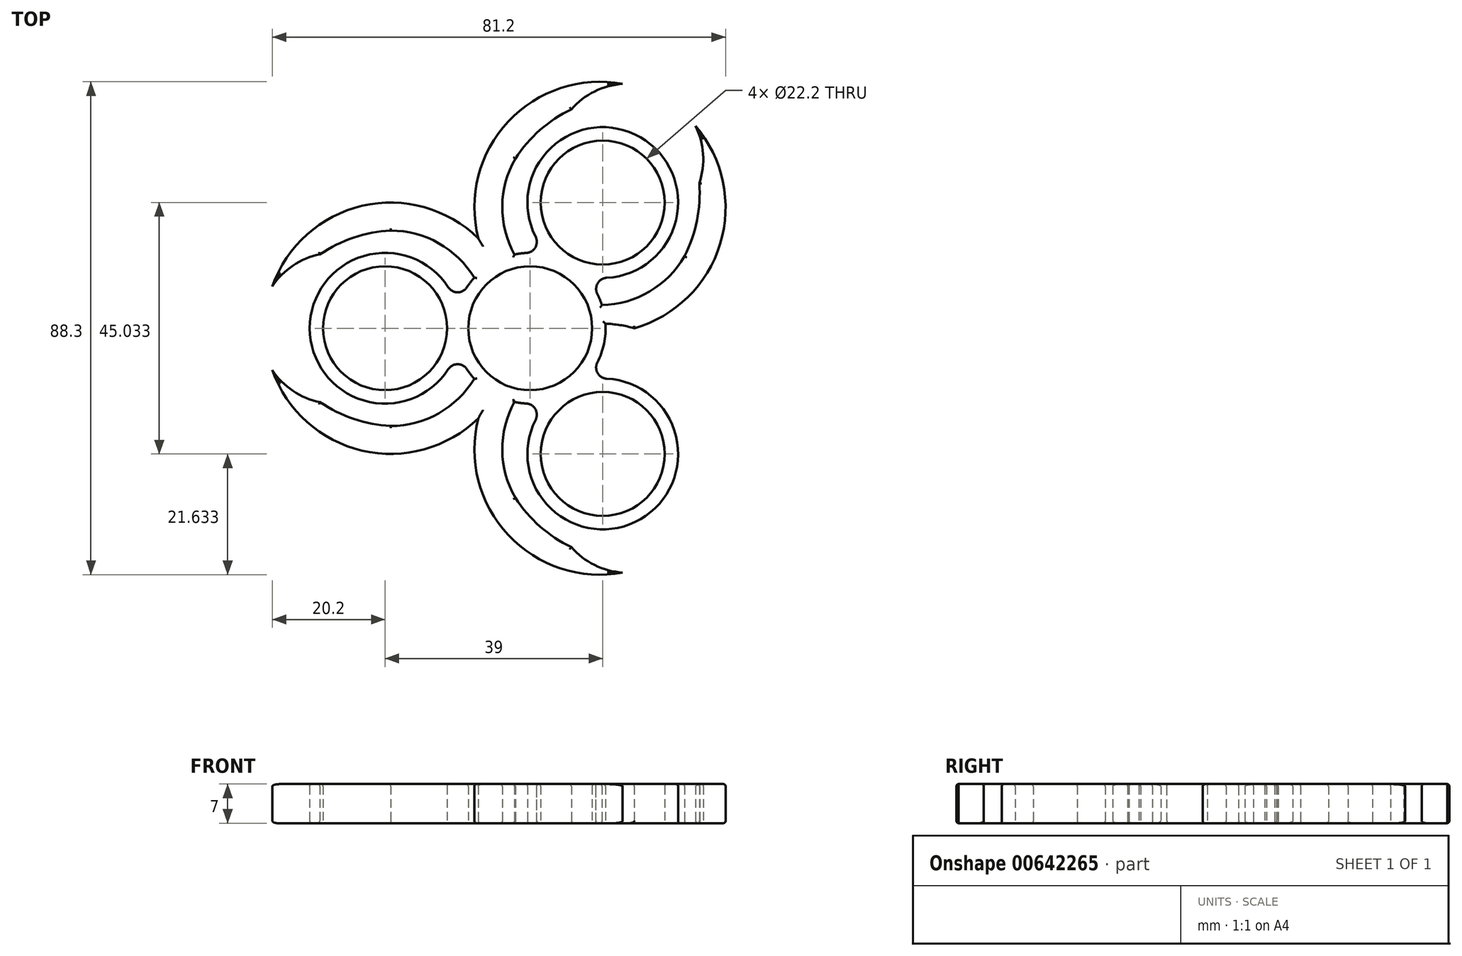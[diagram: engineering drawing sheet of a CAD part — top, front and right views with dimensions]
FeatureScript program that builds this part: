
annotation { "Feature Type Name" : "Feature", "Feature Type Description" : "" }
export const myFeature = defineFeature(function(context is Context, id is Id, definition is map)
    precondition{}
    {
        {
            var Q0;
            Q0=qCreatedBy(makeId("Top.planeOp"),FACE);
            var sketch = newSketch(context, id + "F0", { "sketchPlane" : qUnion([Q0])});
            skLineSegment(sketch, "E0", {"start": v(0, 0) * mm, "end": v(-25, 0) * mm, "construction": true});
            skArc(sketch, "E1", {"start": v(-25, -17.5) * mm, "mid": v(-7.5, 0) * mm, "end": v(-25, 17.5) * mm});
            skCircle(sketch, "E2", {"center": v(-25, 0) * mm, "radius": 22.5 * mm});
            skLineSegment(sketch, "E3", {"start": v(-25, 0) * mm, "end": v(-25, 22.5) * mm, "construction": true});
            skLineSegment(sketch, "E4", {"start": v(-25, 0) * mm, "end": v(-25, -22.5) * mm, "construction": true});
            skLineSegment(sketch, "E5", {"start": v(-25, 0) * mm, "end": v(-47.5, 0) * mm, "construction": true});
            skArc(sketch, "E6", {"start": v(-25, 17.5) * mm, "mid": v(-38.99, 12.27) * mm, "end": v(-47.5, 0) * mm});
            skArc(sketch, "E7.MirrorCS", {"start": v(-25, -17.5) * mm, "mid": v(-38.99, -12.27) * mm, "end": v(-47.5, 0) * mm});
            skArc(sketch, "E8.1.0", {"start": v(27.66, -12.9) * mm, "mid": v(30.12, -27.63) * mm, "end": v(23.75, -41.14) * mm});
            skLineSegment(sketch, "E8.1.1", {"start": v(12.5, -21.65) * mm, "end": v(-6.99, -32.9) * mm, "construction": true});
            skArc(sketch, "E8.1.2", {"start": v(-2.66, -30.4) * mm, "mid": v(8.87, -39.9) * mm, "end": v(23.75, -41.14) * mm});
            skLineSegment(sketch, "E8.1.3", {"start": v(12.5, -21.65) * mm, "end": v(23.75, -41.14) * mm, "construction": true});
            skArc(sketch, "E8.1.4", {"start": v(27.66, -12.9) * mm, "mid": v(3.75, -6.5) * mm, "end": v(-2.66, -30.4) * mm});
            skArc(sketch, "E8.1.5", {"start": v(-9.31, -16.13) * mm, "mid": v(33.52, -29.66) * mm, "end": v(-7.45, -11.26) * mm});
            skLineSegment(sketch, "E8.1.6", {"start": v(12.5, -21.65) * mm, "end": v(31.99, -10.4) * mm, "construction": true});
            skArc(sketch, "E8.2.0", {"start": v(-2.66, 30.4) * mm, "mid": v(8.87, 39.9) * mm, "end": v(23.75, 41.14) * mm});
            skLineSegment(sketch, "E8.2.1", {"start": v(12.5, 21.65) * mm, "end": v(31.99, 10.4) * mm, "construction": true});
            skArc(sketch, "E8.2.2", {"start": v(27.66, 12.9) * mm, "mid": v(30.12, 27.63) * mm, "end": v(23.75, 41.14) * mm});
            skLineSegment(sketch, "E8.2.3", {"start": v(12.5, 21.65) * mm, "end": v(23.75, 41.14) * mm, "construction": true});
            skArc(sketch, "E8.2.4", {"start": v(-2.66, 30.4) * mm, "mid": v(3.75, 6.5) * mm, "end": v(27.66, 12.9) * mm});
            skArc(sketch, "E8.2.5", {"start": v(-7.45, 11.26) * mm, "mid": v(1.25, 2.17) * mm, "end": v(13.47, -0.83) * mm});
            skLineSegment(sketch, "E8.2.6", {"start": v(12.5, 21.65) * mm, "end": v(-6.99, 32.9) * mm, "construction": true});
            skPoint(sketch, "E8.center", {"position": v(0, 0) * mm});
            skCircle(sketch, "E9.0.0", {"center": v(0, 0) * mm, "radius": 13.5 * mm});
            skCircle(sketch, "E10.0.0", {"center": v(-35, 0) * mm, "radius": 13.5 * mm});
            skCircle(sketch, "E11.0.0", {"center": v(17.5, 30.31) * mm, "radius": 13.5 * mm});
            skCircle(sketch, "E12.0.0", {"center": v(17.5, -30.31) * mm, "radius": 13.5 * mm});
            skCircle(sketch, "E13.0", {"center": v(0, 0) * mm, "radius": 11 * mm});
            skArc(sketch, "E14.trimOffspring", {"start": v(18.62, 0) * mm, "mid": v(23.75, 41.14) * mm, "end": v(-9.31, 16.13) * mm});
            skSolve(sketch);
        }
        {
            var Q0;
            Q0=qCreatedBy(makeId("Top.planeOp"),FACE);
            var sketch = newSketch(context, id + "F1", { "sketchPlane" : qUnion([Q0])});
            skCircle(sketch, "E15", {"center": v(0, 0) * mm, "radius": 11.1 * mm});
            skCircle(sketch, "E16", {"center": v(0, 0) * mm, "radius": 13.5 * mm});
            skLineSegment(sketch, "E17", {"start": v(0, 0) * mm, "end": v(-26, 0) * mm, "construction": true});
            skCircle(sketch, "E18", {"center": v(-26, 0) * mm, "radius": 11.1 * mm});
            skCircle(sketch, "E19", {"center": v(-26, 0) * mm, "radius": 13.5 * mm});
            skCircle(sketch, "E20.1.0", {"center": v(13, -22.52) * mm, "radius": 11.1 * mm});
            skCircle(sketch, "E20.1.1", {"center": v(13, -22.52) * mm, "radius": 13.5 * mm});
            skCircle(sketch, "E20.2.0", {"center": v(13, 22.52) * mm, "radius": 11.1 * mm});
            skCircle(sketch, "E20.2.1", {"center": v(13, 22.52) * mm, "radius": 13.5 * mm});
            skSolve(sketch);
        }
        {
            var Q0;
            Q0=makeQuery(id+"F1.imprint","IMPRINT",FACE,{"disambiguationData":[TD([[makeQuery(id+"F1.imprint","IMPRINT",EDGE,{"derivedFrom":sQuery(id+"F1.wireOp",EDGE,"E15")}),-1.0]])]});
            var Q1;
            {var subQ0=sQuery(id+"F1.wireOp",EDGE,"E19");var subQ1=sQuery(id+"F1.wireOp",EDGE,"E16");var subQ2=makeQuery(id+"F1.imprint","INTERSECT",VERTEX,{"disambiguationData":[OD(0.0)],"derivedFrom":[subQ1,subQ0]});Q1=makeQuery(id+"F1.imprint","IMPRINT",FACE,{"disambiguationData":[TD([[makeQuery(id+"F1.imprint","IMPRINT",EDGE,{"disambiguationData":[TD([[subQ2,-1.0]])],"derivedFrom":subQ1}),1.0]])]});}
            var Q2;
            Q2=makeQuery(id+"F1.imprint","IMPRINT",FACE,{"disambiguationData":[TD([[makeQuery(id+"F1.imprint","IMPRINT",EDGE,{"derivedFrom":sQuery(id+"F1.wireOp",EDGE,"E18")}),-1.0]])]});
            var Q3;
            {var subQ0=sQuery(id+"F1.wireOp",EDGE,"E20.2.1");var subQ1=sQuery(id+"F1.wireOp",EDGE,"E16");var subQ2=makeQuery(id+"F1.imprint","INTERSECT",VERTEX,{"disambiguationData":[OD(0.0)],"derivedFrom":[subQ1,subQ0]});Q3=makeQuery(id+"F1.imprint","IMPRINT",FACE,{"disambiguationData":[TD([[makeQuery(id+"F1.imprint","IMPRINT",EDGE,{"disambiguationData":[TD([[subQ2,1.0]])],"derivedFrom":subQ1}),1.0]])]});}
            var Q4;
            Q4=makeQuery(id+"F1.imprint","IMPRINT",FACE,{"disambiguationData":[TD([[makeQuery(id+"F1.imprint","IMPRINT",EDGE,{"derivedFrom":sQuery(id+"F1.wireOp",EDGE,"E20.2.0")}),-1.0]])]});
            var Q5;
            Q5=makeQuery(id+"F1.imprint","IMPRINT",FACE,{"disambiguationData":[TD([[makeQuery(id+"F1.imprint","IMPRINT",EDGE,{"derivedFrom":sQuery(id+"F1.wireOp",EDGE,"E20.1.0")}),-1.0]])]});
            var Q6;
            {var subQ0=sQuery(id+"F1.wireOp",EDGE,"E20.1.1");var subQ1=sQuery(id+"F1.wireOp",EDGE,"E16");var subQ2=makeQuery(id+"F1.imprint","INTERSECT",VERTEX,{"disambiguationData":[OD(0.0)],"derivedFrom":[subQ1,subQ0]});Q6=makeQuery(id+"F1.imprint","IMPRINT",FACE,{"disambiguationData":[TD([[makeQuery(id+"F1.imprint","IMPRINT",EDGE,{"disambiguationData":[TD([[subQ2,-1.0]])],"derivedFrom":subQ1}),1.0]])]});}
            extrude(context, id + "F2", {"entities" : qUnion([Q0, Q1, Q2, Q3, Q4, Q5, Q6]), "depth" : 7 * mm, "offsetDistance" : 25 * mm});
        }
        {
            var Q0;
            {var subQ5=sQuery(id+"F0.wireOp",EDGE,"E6");var subQ6=sQuery(id+"F0.wireOp",EDGE,"E1");var subQ7=makeQuery(id+"F0.imprint","INTERSECT",VERTEX,{"derivedFrom":[subQ6,subQ5]});Q0=makeQuery(id+"F0.imprint","IMPRINT",FACE,{"disambiguationData":[TD([[makeQuery(id+"F0.imprint","IMPRINT",EDGE,{"disambiguationData":[TD([[subQ7,1.0]])],"derivedFrom":subQ6}),-1.0]])]});}
            var Q1;
            {var subQ0=sQuery(id+"F0.wireOp",EDGE,"E7.MirrorCS");var subQ1=sQuery(id+"F0.wireOp",EDGE,"E1");var subQ2=makeQuery(id+"F0.imprint","INTERSECT",VERTEX,{"derivedFrom":[subQ1,subQ0]});Q1=makeQuery(id+"F0.imprint","IMPRINT",FACE,{"disambiguationData":[TD([[makeQuery(id+"F0.imprint","IMPRINT",EDGE,{"disambiguationData":[TD([[subQ2,-1.0]])],"derivedFrom":subQ1}),-1.0]])]});}
            var Q2;
            Q2=makeQuery(id+"F1.imprint","IMPRINT",FACE,{"disambiguationData":[TD([[makeQuery(id+"F1.imprint","IMPRINT",EDGE,{"derivedFrom":sQuery(id+"F1.wireOp",EDGE,"E18")}),-1.0]])]});
            var Q3;
            {var subQ1=sQuery(id+"F0.wireOp",EDGE,"E2");var subQ9=sQuery(id+"F0.wireOp",EDGE,"E14.trimOffspring");var subQ10=makeQuery(id+"F0.imprint","INTERSECT",VERTEX,{"derivedFrom":[subQ1,subQ9]});Q3=makeQuery(id+"F0.imprint","IMPRINT",FACE,{"disambiguationData":[TD([[makeQuery(id+"F0.imprint","IMPRINT",EDGE,{"disambiguationData":[TD([[subQ10,1.0]])],"derivedFrom":subQ1}),-1.0]])]});}
            var Q4;
            {var subQ5=sQuery(id+"F0.wireOp",EDGE,"E14.trimOffspring");var subQ9=sQuery(id+"F0.wireOp",EDGE,"E8.1.5");var subQ11=makeQuery(id+"F0.imprint","INTERSECT",VERTEX,{"derivedFrom":[subQ9,subQ5]});Q4=makeQuery(id+"F0.imprint","IMPRINT",FACE,{"disambiguationData":[TD([[makeQuery(id+"F0.imprint","IMPRINT",EDGE,{"disambiguationData":[TD([[subQ11,-1.0]])],"derivedFrom":subQ9}),-1.0]])]});}
            var Q5;
            Q5=makeQuery(id+"F1.imprint","IMPRINT",FACE,{"disambiguationData":[TD([[makeQuery(id+"F1.imprint","IMPRINT",EDGE,{"derivedFrom":sQuery(id+"F1.wireOp",EDGE,"E20.2.0")}),-1.0]])]});
            var Q6;
            {var subQ6=sQuery(id+"F0.wireOp",EDGE,"E8.1.4");var subQ7=sQuery(id+"F0.wireOp",EDGE,"E8.1.0");var subQ8=makeQuery(id+"F0.imprint","INTERSECT",VERTEX,{"derivedFrom":[subQ7,subQ6]});Q6=makeQuery(id+"F0.imprint","IMPRINT",FACE,{"disambiguationData":[TD([[makeQuery(id+"F0.imprint","IMPRINT",EDGE,{"disambiguationData":[TD([[subQ8,-1.0]])],"derivedFrom":subQ7}),1.0]])]});}
            var Q7;
            {var subQ0=sQuery(id+"F0.wireOp",EDGE,"E8.1.5");var subQ1=sQuery(id+"F0.wireOp",EDGE,"E2");var subQ2=makeQuery(id+"F0.imprint","INTERSECT",VERTEX,{"disambiguationData":[OD(0.0)],"derivedFrom":[subQ1,subQ0]});Q7=makeQuery(id+"F0.imprint","IMPRINT",FACE,{"disambiguationData":[TD([[makeQuery(id+"F0.imprint","IMPRINT",EDGE,{"disambiguationData":[TD([[subQ2,-1.0]])],"derivedFrom":subQ1}),-1.0]])]});}
            var Q8;
            Q8=makeQuery(id+"F1.imprint","IMPRINT",FACE,{"disambiguationData":[TD([[makeQuery(id+"F1.imprint","IMPRINT",EDGE,{"derivedFrom":sQuery(id+"F1.wireOp",EDGE,"E20.1.0")}),-1.0]])]});
            extrude(context, id + "F3", {"entities" : qUnion([Q0, Q1, Q2, Q3, Q4, Q5, Q6, Q7, Q8]), "operationType" : NewBodyOperationType.ADD, "depth" : 7 * mm, "offsetDistance" : 25 * mm});
        }
        {
            var Q0;
            {var subQ0=sQuery(id+"F1.wireOp",EDGE,"E19");var subQ1=sQuery(id+"F1.wireOp",EDGE,"E16");Q0=makeQuery(id+"F2.opExtrude","SWEPT_EDGE",EDGE,{"disambiguationData":[OSD([subQ1,subQ0]),TDD([makeQuery(id+"F1.imprint","INTERSECT",VERTEX,{"disambiguationData":[OD(1.0)],"derivedFrom":[subQ1,subQ0]})])]});}
            var Q1;
            {var subQ0=sQuery(id+"F1.wireOp",EDGE,"E20.1.1");var subQ1=sQuery(id+"F1.wireOp",EDGE,"E16");Q1=makeQuery(id+"F2.opExtrude","SWEPT_EDGE",EDGE,{"disambiguationData":[OSD([subQ1,subQ0]),TDD([makeQuery(id+"F1.imprint","INTERSECT",VERTEX,{"disambiguationData":[OD(0.0)],"derivedFrom":[subQ1,subQ0]})])]});}
            var Q2;
            {var subQ0=sQuery(id+"F1.wireOp",EDGE,"E20.1.1");var subQ1=sQuery(id+"F1.wireOp",EDGE,"E16");Q2=makeQuery(id+"F2.opExtrude","SWEPT_EDGE",EDGE,{"disambiguationData":[OSD([subQ1,subQ0]),TDD([makeQuery(id+"F1.imprint","INTERSECT",VERTEX,{"disambiguationData":[OD(1.0)],"derivedFrom":[subQ1,subQ0]})])]});}
            var Q3;
            {var subQ0=sQuery(id+"F1.wireOp",EDGE,"E20.2.1");var subQ1=sQuery(id+"F1.wireOp",EDGE,"E16");Q3=makeQuery(id+"F2.opExtrude","SWEPT_EDGE",EDGE,{"disambiguationData":[OSD([subQ1,subQ0]),TDD([makeQuery(id+"F1.imprint","INTERSECT",VERTEX,{"disambiguationData":[OD(1.0)],"derivedFrom":[subQ1,subQ0]})])]});}
            var Q4;
            {var subQ0=sQuery(id+"F1.wireOp",EDGE,"E19");var subQ1=sQuery(id+"F1.wireOp",EDGE,"E16");Q4=makeQuery(id+"F2.opExtrude","SWEPT_EDGE",EDGE,{"disambiguationData":[OSD([subQ1,subQ0]),TDD([makeQuery(id+"F1.imprint","INTERSECT",VERTEX,{"disambiguationData":[OD(0.0)],"derivedFrom":[subQ1,subQ0]})])]});}
            var Q5;
            {var subQ0=sQuery(id+"F1.wireOp",EDGE,"E20.2.1");var subQ1=sQuery(id+"F1.wireOp",EDGE,"E16");Q5=makeQuery(id+"F2.opExtrude","SWEPT_EDGE",EDGE,{"disambiguationData":[OSD([subQ1,subQ0]),TDD([makeQuery(id+"F1.imprint","INTERSECT",VERTEX,{"disambiguationData":[OD(0.0)],"derivedFrom":[subQ1,subQ0]})])]});}
            fillet(context, id + "F4", {"entities" : qUnion([Q0, Q1, Q2, Q3, Q4, Q5]), "radius" : 2 * mm, "tangentPropagation" : true, "allowEdgeOverflow" : false});
        }
        {
            var Q0;
            {var subQ0=sQuery(id+"F0.wireOp",EDGE,"E14.trimOffspring");var subQ1=sQuery(id+"F0.wireOp",EDGE,"E12.0.0");var subQ2=sQuery(id+"F0.wireOp",EDGE,"E11.0.0");var subQ3=sQuery(id+"F0.wireOp",EDGE,"E9.0.0");var subQ4=sQuery(id+"F0.wireOp",EDGE,"E8.2.4");var subQ5=sQuery(id+"F0.wireOp",EDGE,"E8.1.5");var subQ6=sQuery(id+"F0.wireOp",EDGE,"E8.1.4");var subQ7=sQuery(id+"F0.wireOp",EDGE,"E10.0.0");var subQ8=sQuery(id+"F0.wireOp",EDGE,"E2");var subQ9=sQuery(id+"F0.wireOp",EDGE,"E1");Q0=makeQuery(id+"F3.boolean.opBoolean","MERGE",FACE,{"derivedFrom":[makeQuery(id+"F2.opExtrude","CAP_FACE",FACE,{"disambiguationData":[OSD([sQuery(id+"F1.wireOp",EDGE,"E15"),sQuery(id+"F1.wireOp",EDGE,"E16")])],"isStart":false}),makeQuery(id+"F3.opExtrude","CAP_FACE",FACE,{"disambiguationData":[OSD([sQuery(id+"F1.wireOp",EDGE,"E18"),sQuery(id+"F1.wireOp",EDGE,"E19")])],"isStart":false}),makeQuery(id+"F3.opExtrude","CAP_FACE",FACE,{"disambiguationData":[OSD([sQuery(id+"F1.wireOp",EDGE,"E20.1.0"),sQuery(id+"F1.wireOp",EDGE,"E20.1.1")])],"isStart":false}),makeQuery(id+"F3.opExtrude","CAP_FACE",FACE,{"disambiguationData":[OSD([sQuery(id+"F1.wireOp",EDGE,"E20.2.0"),sQuery(id+"F1.wireOp",EDGE,"E20.2.1")])],"isStart":false}),makeQuery(id+"F3.opExtrude","CAP_FACE",FACE,{"disambiguationData":[OSD([subQ9,subQ8,sQuery(id+"F0.wireOp",EDGE,"E7.MirrorCS"),sQuery(id+"F0.wireOp",EDGE,"E8.1.2"),subQ6,subQ5,subQ3,subQ7,subQ1])],"isStart":false}),makeQuery(id+"F3.opExtrude","CAP_FACE",FACE,{"disambiguationData":[OSD([subQ9,subQ8,sQuery(id+"F0.wireOp",EDGE,"E6"),sQuery(id+"F0.wireOp",EDGE,"E8.2.0"),subQ4,subQ3,subQ7,subQ2,subQ0])],"isStart":false}),makeQuery(id+"F3.opExtrude","CAP_FACE",FACE,{"disambiguationData":[OSD([sQuery(id+"F0.wireOp",EDGE,"E8.1.0"),subQ6,subQ5,sQuery(id+"F0.wireOp",EDGE,"E8.2.2"),subQ4,subQ3,subQ2,subQ1,subQ0])],"isStart":false})]});}
            var Q1;
            {var subQ0=sQuery(id+"F0.wireOp",EDGE,"E2");Q1=makeQuery(id+"F3.opExtrude","CAP_EDGE",EDGE,{"disambiguationData":[OSD([subQ0]),TDD([makeQuery(id+"F0.imprint","IMPRINT",EDGE,{"disambiguationData":[TD([[makeQuery(id+"F0.imprint","INTERSECT",VERTEX,{"disambiguationData":[OD(0.0)],"derivedFrom":[subQ0,sQuery(id+"F0.wireOp",EDGE,"E8.1.5")]}),1.0]])],"derivedFrom":subQ0})])],"isStart":true});}
            var Q2;
            {var subQ0=sQuery(id+"F1.wireOp",EDGE,"E19");var subQ1=sQuery(id+"F0.wireOp",EDGE,"E14.trimOffspring");var subQ9=sQuery(id+"F0.wireOp",EDGE,"E2");Q2=makeQuery(id+"F3.boolean.opBoolean","SPLIT",EDGE,{"disambiguationData":[TD([makeQuery(id+"F3.opExtrude","SWEPT_FACE",FACE,{"disambiguationData":[OSD([subQ9]),TDD([makeQuery(id+"F0.imprint","IMPRINT",EDGE,{"disambiguationData":[TD([[makeQuery(id+"F0.imprint","INTERSECT",VERTEX,{"derivedFrom":[subQ9,subQ1]}),-1.0]])],"derivedFrom":subQ9})])]})])],"derivedFrom":makeQuery(id+"F3.opExtrude","CAP_EDGE",EDGE,{"disambiguationData":[OSD([subQ0])],"isStart":true})});}
            var Q3;
            {var subQ0=sQuery(id+"F0.wireOp",EDGE,"E2");Q3=makeQuery(id+"F3.opExtrude","CAP_EDGE",EDGE,{"disambiguationData":[OSD([subQ0]),TDD([makeQuery(id+"F0.imprint","IMPRINT",EDGE,{"disambiguationData":[TD([[makeQuery(id+"F0.imprint","INTERSECT",VERTEX,{"derivedFrom":[subQ0,sQuery(id+"F0.wireOp",EDGE,"E14.trimOffspring")]}),-1.0]])],"derivedFrom":subQ0})])],"isStart":true});}
            var Q4;
            {var subQ0=sQuery(id+"F0.wireOp",EDGE,"E14.trimOffspring");Q4=makeQuery(id+"F3.opExtrude","CAP_EDGE",EDGE,{"disambiguationData":[OSD([subQ0]),TDD([makeQuery(id+"F0.imprint","IMPRINT",EDGE,{"disambiguationData":[TD([[makeQuery(id+"F0.imprint","INTERSECT",VERTEX,{"derivedFrom":[sQuery(id+"F0.wireOp",EDGE,"E2"),subQ0]}),1.0]])],"derivedFrom":subQ0})])],"isStart":true});}
            var Q5;
            {var subQ0=sQuery(id+"F1.wireOp",EDGE,"E20.2.1");var subQ1=sQuery(id+"F0.wireOp",EDGE,"E14.trimOffspring");var subQ6=sQuery(id+"F0.wireOp",EDGE,"E8.1.5");Q5=makeQuery(id+"F3.boolean.opBoolean","SPLIT",EDGE,{"disambiguationData":[TD([makeQuery(id+"F3.opExtrude","SWEPT_FACE",FACE,{"disambiguationData":[OSD([subQ1]),TDD([makeQuery(id+"F0.imprint","IMPRINT",EDGE,{"disambiguationData":[TD([[makeQuery(id+"F0.imprint","INTERSECT",VERTEX,{"derivedFrom":[subQ6,subQ1]}),-1.0]])],"derivedFrom":subQ1})])]})])],"derivedFrom":makeQuery(id+"F3.opExtrude","CAP_EDGE",EDGE,{"disambiguationData":[OSD([subQ0])],"isStart":true})});}
            var Q6;
            Q6=makeQuery(id+"F3.opExtrude","CAP_EDGE",EDGE,{"disambiguationData":[OSD([sQuery(id+"F0.wireOp",EDGE,"E8.2.2")])],"isStart":true});
            var Q7;
            Q7=makeQuery(id+"F3.opExtrude","CAP_EDGE",EDGE,{"disambiguationData":[OSD([sQuery(id+"F0.wireOp",EDGE,"E8.2.0")])],"isStart":true});
            var Q8;
            {var subQ0=sQuery(id+"F0.wireOp",EDGE,"E7.MirrorCS");var subQ1=sQuery(id+"F0.wireOp",EDGE,"E1");var subQ9=sQuery(id+"F1.wireOp",EDGE,"E16");Q8=makeQuery(id+"F3.boolean.opBoolean","SPLIT",EDGE,{"disambiguationData":[TD([makeQuery(id+"F3.opExtrude","SWEPT_FACE",FACE,{"disambiguationData":[OSD([subQ1]),TDD([makeQuery(id+"F0.imprint","IMPRINT",EDGE,{"disambiguationData":[TD([[makeQuery(id+"F0.imprint","INTERSECT",VERTEX,{"derivedFrom":[subQ1,subQ0]}),-1.0]])],"derivedFrom":subQ1})])]})])],"derivedFrom":makeQuery(id+"F2.opExtrude","CAP_EDGE",EDGE,{"disambiguationData":[OSD([subQ9])],"isStart":true})});}
            var Q9;
            {var subQ4=sQuery(id+"F0.wireOp",EDGE,"E8.2.4");var subQ8=sQuery(id+"F1.wireOp",EDGE,"E16");var subQ9=sQuery(id+"F0.wireOp",EDGE,"E8.2.0");Q9=makeQuery(id+"F3.boolean.opBoolean","SPLIT",EDGE,{"disambiguationData":[TD([makeQuery(id+"F3.opExtrude","SWEPT_FACE",FACE,{"disambiguationData":[OSD([subQ4]),TDD([makeQuery(id+"F0.imprint","IMPRINT",EDGE,{"disambiguationData":[TD([[makeQuery(id+"F0.imprint","INTERSECT",VERTEX,{"derivedFrom":[subQ9,subQ4]}),-1.0]])],"derivedFrom":subQ4})])]})])],"derivedFrom":makeQuery(id+"F2.opExtrude","CAP_EDGE",EDGE,{"disambiguationData":[OSD([subQ8])],"isStart":true})});}
            var Q10;
            {var subQ0=sQuery(id+"F0.wireOp",EDGE,"E1");Q10=makeQuery(id+"F3.opExtrude","CAP_EDGE",EDGE,{"disambiguationData":[OSD([subQ0]),TDD([makeQuery(id+"F0.imprint","IMPRINT",EDGE,{"disambiguationData":[TD([[makeQuery(id+"F0.imprint","INTERSECT",VERTEX,{"derivedFrom":[subQ0,sQuery(id+"F0.wireOp",EDGE,"E7.MirrorCS")]}),-1.0]])],"derivedFrom":subQ0})])],"isStart":true});}
            var Q11;
            Q11=makeQuery(id+"F3.opExtrude","CAP_EDGE",EDGE,{"disambiguationData":[OSD([sQuery(id+"F0.wireOp",EDGE,"E7.MirrorCS")])],"isStart":true});
            var Q12;
            {var subQ0=sQuery(id+"F1.wireOp",EDGE,"E19");var subQ9=sQuery(id+"F0.wireOp",EDGE,"E6");Q12=makeQuery(id+"F3.boolean.opBoolean","SPLIT",EDGE,{"disambiguationData":[TD([makeQuery(id+"F3.opExtrude","SWEPT_FACE",FACE,{"disambiguationData":[OSD([subQ9])]})])],"derivedFrom":makeQuery(id+"F3.opExtrude","CAP_EDGE",EDGE,{"disambiguationData":[OSD([subQ0])],"isStart":true})});}
            var Q13;
            {var subQ0=sQuery(id+"F0.wireOp",EDGE,"E1");Q13=makeQuery(id+"F3.opExtrude","CAP_EDGE",EDGE,{"disambiguationData":[OSD([subQ0]),TDD([makeQuery(id+"F0.imprint","IMPRINT",EDGE,{"disambiguationData":[TD([[makeQuery(id+"F0.imprint","INTERSECT",VERTEX,{"derivedFrom":[subQ0,sQuery(id+"F0.wireOp",EDGE,"E6")]}),1.0]])],"derivedFrom":subQ0})])],"isStart":true});}
            var Q14;
            Q14=makeQuery(id+"F3.opExtrude","CAP_EDGE",EDGE,{"disambiguationData":[OSD([sQuery(id+"F0.wireOp",EDGE,"E6")])],"isStart":true});
            var Q15;
            {var subQ0=sQuery(id+"F0.wireOp",EDGE,"E14.trimOffspring");Q15=makeQuery(id+"F3.opExtrude","CAP_EDGE",EDGE,{"disambiguationData":[OSD([subQ0]),TDD([makeQuery(id+"F0.imprint","IMPRINT",EDGE,{"disambiguationData":[TD([[makeQuery(id+"F0.imprint","INTERSECT",VERTEX,{"derivedFrom":[sQuery(id+"F0.wireOp",EDGE,"E8.1.5"),subQ0]}),-1.0]])],"derivedFrom":subQ0})])],"isStart":true});}
            var Q16;
            {var subQ0=sQuery(id+"F0.wireOp",EDGE,"E8.1.5");Q16=makeQuery(id+"F3.opExtrude","CAP_EDGE",EDGE,{"disambiguationData":[OSD([subQ0]),TDD([makeQuery(id+"F0.imprint","IMPRINT",EDGE,{"disambiguationData":[TD([[makeQuery(id+"F0.imprint","INTERSECT",VERTEX,{"derivedFrom":[subQ0,sQuery(id+"F0.wireOp",EDGE,"E14.trimOffspring")]}),1.0]])],"derivedFrom":subQ0})])],"isStart":true});}
            var Q17;
            {var subQ0=sQuery(id+"F0.wireOp",EDGE,"E8.1.4");Q17=makeQuery(id+"F3.opExtrude","CAP_EDGE",EDGE,{"disambiguationData":[OSD([subQ0]),TDD([makeQuery(id+"F0.imprint","IMPRINT",EDGE,{"disambiguationData":[TD([[makeQuery(id+"F0.imprint","INTERSECT",VERTEX,{"derivedFrom":[sQuery(id+"F0.wireOp",EDGE,"E8.1.2"),subQ0]}),1.0]])],"derivedFrom":subQ0})])],"isStart":true});}
            var Q18;
            Q18=makeQuery(id+"F3.opExtrude","CAP_EDGE",EDGE,{"disambiguationData":[OSD([sQuery(id+"F0.wireOp",EDGE,"E8.1.2")])],"isStart":true});
            var Q19;
            Q19=makeQuery(id+"F3.opExtrude","CAP_EDGE",EDGE,{"disambiguationData":[OSD([sQuery(id+"F0.wireOp",EDGE,"E8.1.0")])],"isStart":true});
            var Q20;
            {var subQ0=sQuery(id+"F0.wireOp",EDGE,"E8.1.4");Q20=makeQuery(id+"F3.opExtrude","CAP_EDGE",EDGE,{"disambiguationData":[OSD([subQ0]),TDD([makeQuery(id+"F0.imprint","IMPRINT",EDGE,{"disambiguationData":[TD([[makeQuery(id+"F0.imprint","INTERSECT",VERTEX,{"derivedFrom":[sQuery(id+"F0.wireOp",EDGE,"E8.1.0"),subQ0]}),-1.0]])],"derivedFrom":subQ0})])],"isStart":true});}
            var Q21;
            {var subQ0=sQuery(id+"F1.wireOp",EDGE,"E20.2.1");var subQ10=sQuery(id+"F0.wireOp",EDGE,"E8.2.0");Q21=makeQuery(id+"F3.boolean.opBoolean","SPLIT",EDGE,{"disambiguationData":[TD([makeQuery(id+"F3.opExtrude","SWEPT_FACE",FACE,{"disambiguationData":[OSD([subQ10])]})])],"derivedFrom":makeQuery(id+"F3.opExtrude","CAP_EDGE",EDGE,{"disambiguationData":[OSD([subQ0])],"isStart":true})});}
            var Q22;
            {var subQ0=sQuery(id+"F0.wireOp",EDGE,"E8.1.5");Q22=makeQuery(id+"F3.opExtrude","CAP_EDGE",EDGE,{"disambiguationData":[OSD([subQ0]),TDD([makeQuery(id+"F0.imprint","IMPRINT",EDGE,{"disambiguationData":[TD([[makeQuery(id+"F0.imprint","INTERSECT",VERTEX,{"disambiguationData":[OD(0.0)],"derivedFrom":[sQuery(id+"F0.wireOp",EDGE,"E2"),subQ0]}),-1.0]])],"derivedFrom":subQ0})])],"isStart":true});}
            var Q23;
            {var subQ0=sQuery(id+"F1.wireOp",EDGE,"E20.1.1");var subQ2=sQuery(id+"F0.wireOp",EDGE,"E8.1.5");var subQ9=sQuery(id+"F0.wireOp",EDGE,"E2");Q23=makeQuery(id+"F3.boolean.opBoolean","SPLIT",EDGE,{"disambiguationData":[TD([makeQuery(id+"F3.opExtrude","SWEPT_FACE",FACE,{"disambiguationData":[OSD([subQ2]),TDD([makeQuery(id+"F0.imprint","IMPRINT",EDGE,{"disambiguationData":[TD([[makeQuery(id+"F0.imprint","INTERSECT",VERTEX,{"disambiguationData":[OD(0.0)],"derivedFrom":[subQ9,subQ2]}),-1.0]])],"derivedFrom":subQ2})])]})])],"derivedFrom":makeQuery(id+"F3.opExtrude","CAP_EDGE",EDGE,{"disambiguationData":[OSD([subQ0])],"isStart":true})});}
            fillet(context, id + "F5", {"entities" : qUnion([Q0, Q1, Q2, Q3, Q4, Q5, Q6, Q7, Q8, Q9, Q10, Q11, Q12, Q13, Q14, Q15, Q16, Q17, Q18, Q19, Q20, Q21, Q22, Q23]), "radius" : .4 * mm, "tangentPropagation" : true, "allowEdgeOverflow" : false});
        }
    });
